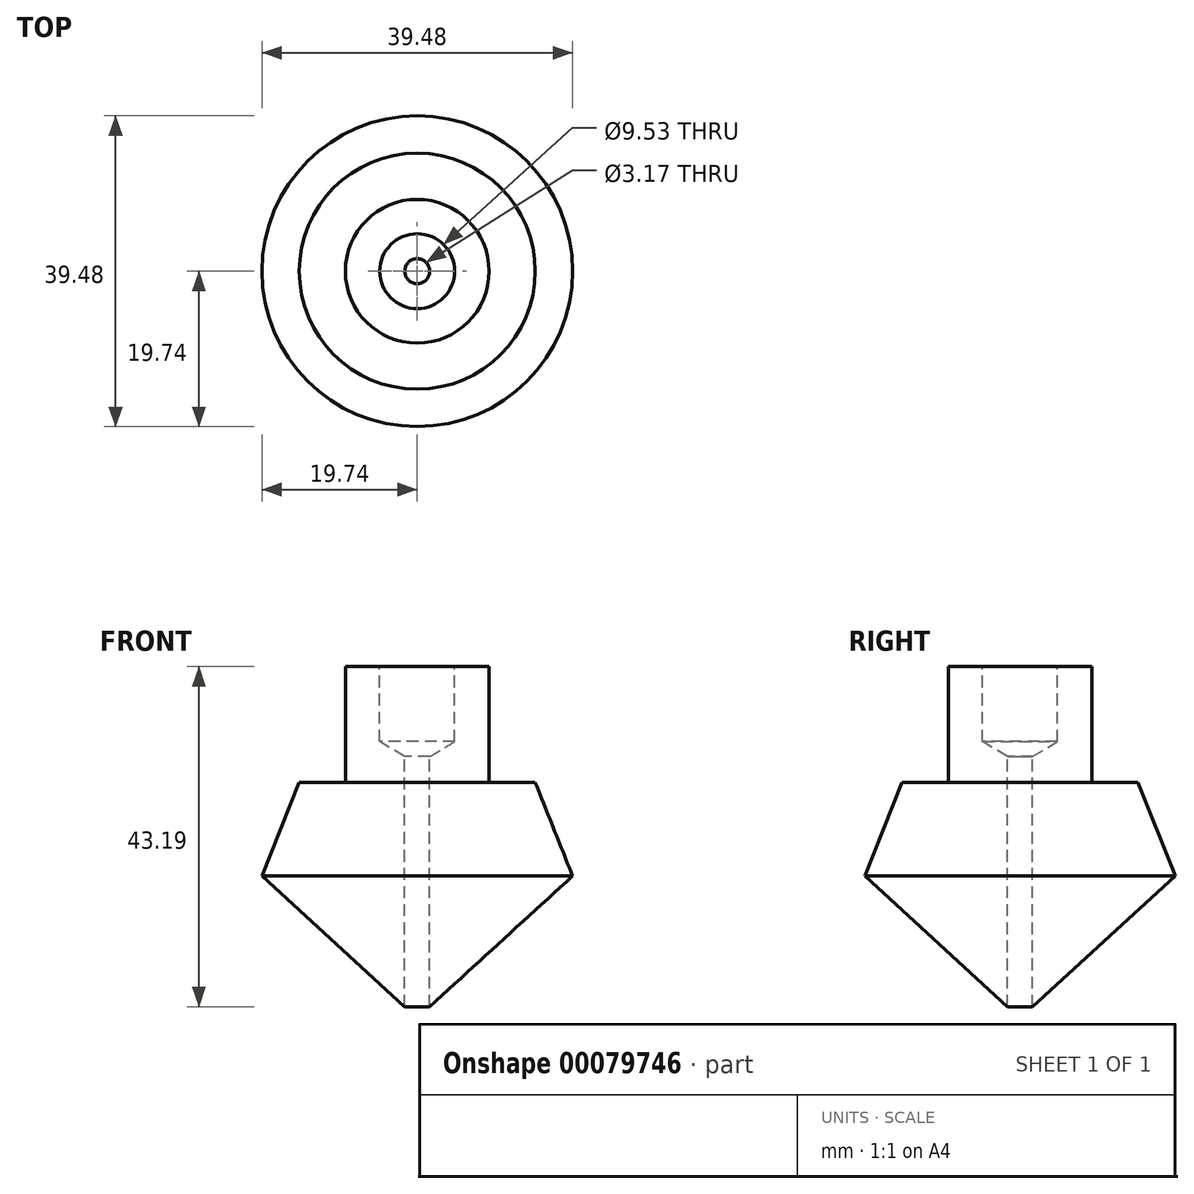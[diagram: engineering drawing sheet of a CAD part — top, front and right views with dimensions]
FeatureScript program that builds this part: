
annotation { "Feature Type Name" : "Feature", "Feature Type Description" : "" }
export const myFeature = defineFeature(function(context is Context, id is Id, definition is map)
    precondition{}
    {
        {
            var Q0;
            Q0=qCreatedBy(makeId("Front.planeOp"),FACE);
            var sketch = newSketch(context, id + "F0", { "sketchPlane" : qUnion([Q0])});
            skLineSegment(sketch, "E0", {"start": v(0, 0) * mm, "end": v(-9.13, 0) * mm});
            skLineSegment(sketch, "E1", {"start": v(0, 0) * mm, "end": v(0, -44.64) * mm});
            skPoint(sketch, "E2.orphan", {"position": v(-31.56, -31.56) * mm});
            skLineSegment(sketch, "E3", {"start": v(-19.74, -26.6) * mm, "end": v(0, -44.64) * mm});
            skPoint(sketch, "E4.end.orphan", {"position": v(-15.78, -38.1) * mm});
            skLineSegment(sketch, "E5", {"start": v(-14.99, -14.69) * mm, "end": v(-19.74, -26.6) * mm});
            skPoint(sketch, "E6.start.orphan", {"position": v(-28.87, 0) * mm});
            skLineSegment(sketch, "E7", {"start": v(-9.13, 0) * mm, "end": v(-9.13, -14.69) * mm});
            skLineSegment(sketch, "E8", {"start": v(-9.13, -14.69) * mm, "end": v(-14.99, -14.69) * mm});
            skSolve(sketch);
        }
        {
            var Q0;
            Q0 = qSketchRegion(id + "F0", true);
            var Q1;
            Q1=sQuery(id+"F0.wireOp",EDGE,"E1");
            revolve(context, id + "F1", {"entities" : qUnion([Q0]), "axis" : qUnion([Q1]), "revolveType" : RevolveType.FULL});
        }
        {
            var Q0;
            Q0=makeQuery(id+"F1.opRevolve","SWEPT_FACE",FACE,{"disambiguationData":[OSD([sQuery(id+"F0.wireOp",EDGE,"E0")])]});
            var sketch = newSketch(context, id + "F2", { "sketchPlane" : qUnion([Q0])});
            skCircle(sketch, "E9", {"center": v(0, 0) * mm, "radius": 3.57 * mm});
            skSolve(sketch);
        }
        {
            var Q0;
            Q0=sQuery(id+"F2.wireOp",VERTEX,"E9.center");
            var Q1;
            Q1=makeQuery(id+"F1.opRevolve","SWEPT_BODY",BODY,{"disambiguationData":[OSD([sQuery(id+"F0.wireOp",EDGE,"cx9EfjWO-7uLF-xhOw-CvJh-ZxXYNTjgoKc3"),sQuery(id+"F0.wireOp",EDGE,"E0"),sQuery(id+"F0.wireOp",EDGE,"E1"),sQuery(id+"F0.wireOp",EDGE,"E4")])]});
            hole(context, id + "F3", {"style" : HoleStyle.SIMPLE, "endStyle" : HoleEndStyle.BLIND, "holeDiameter" : 9.52 * mm, "holeDepth" : 9.52 * mm, "locations" : qUnion([Q0]), "scope" : qUnion([Q1])});
        }
        {
            var Q0;
            Q0=qCreatedBy(makeId("Top.planeOp"),FACE);
            var sketch = newSketch(context, id + "F4", { "sketchPlane" : qUnion([Q0])});
            skCircle(sketch, "E10", {"center": v(0, 0) * mm, "radius": 1.59 * mm});
            skSolve(sketch);
        }
        {
            var Q0;
            Q0 = qSketchRegion(id + "F4", true);
            extrude(context, id + "F5", {"entities" : qUnion([Q0]), "operationType" : NewBodyOperationType.REMOVE, "oppositeDirection" : true, "depth" : 48.27 * mm});
        }
    });
